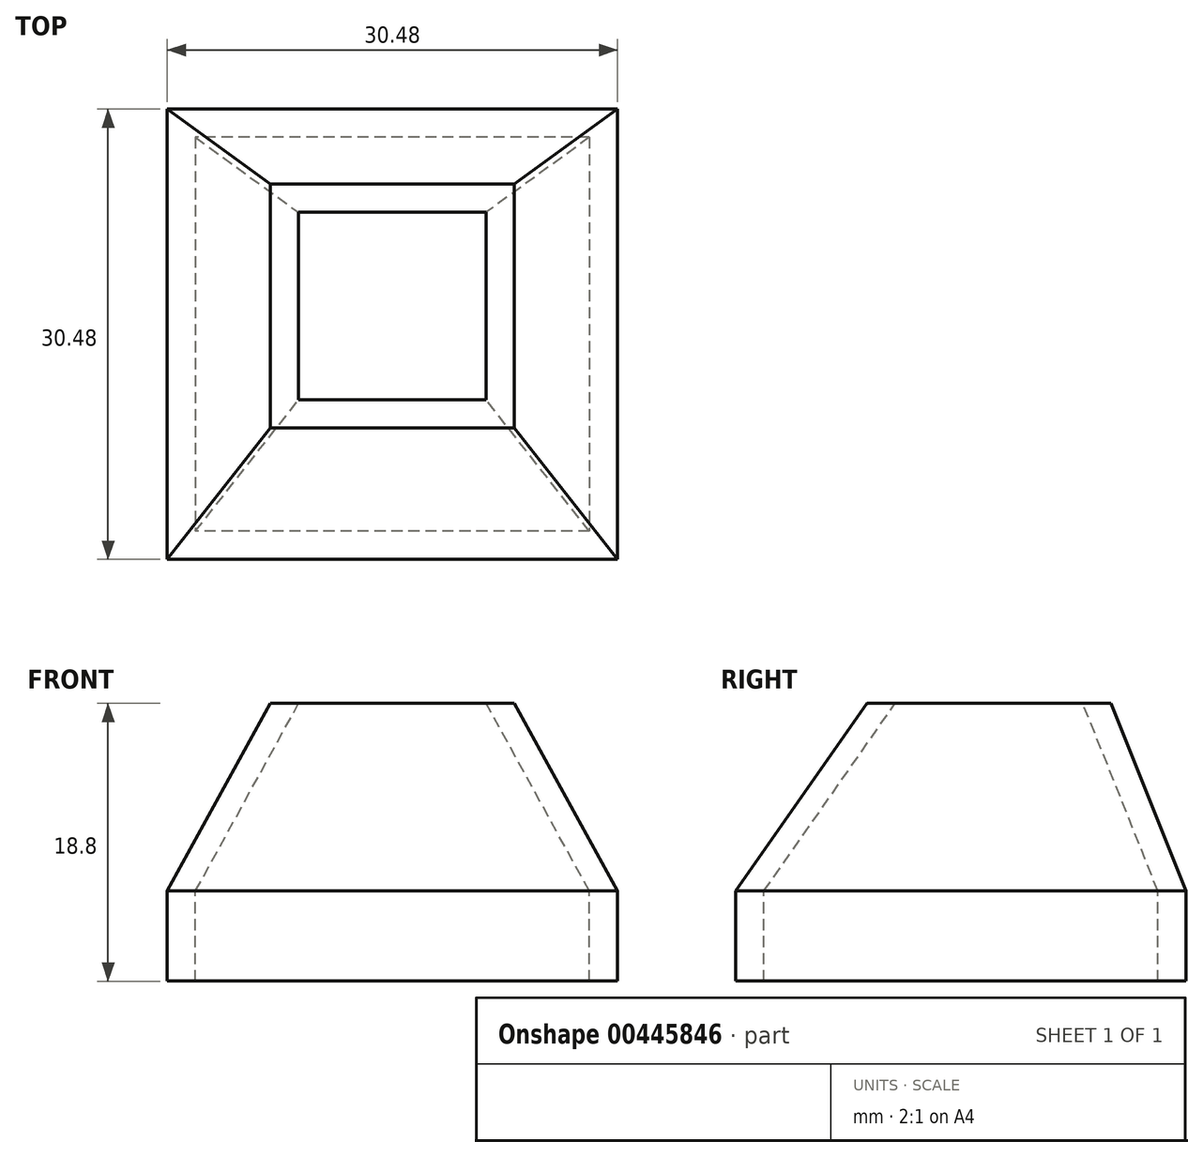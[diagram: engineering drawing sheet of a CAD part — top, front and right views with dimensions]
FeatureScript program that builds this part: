
annotation { "Feature Type Name" : "Feature", "Feature Type Description" : "" }
export const myFeature = defineFeature(function(context is Context, id is Id, definition is map)
    precondition{}
    {
        {
            var Q0;
            Q0=qCreatedBy(makeId("Top.planeOp"),FACE);
            var sketch = newSketch(context, id + "F0", { "sketchPlane" : qUnion([Q0])});
            skLineSegment(sketch, "E0.bottom", {"start": v(13.33, 13.34) * mm, "end": v(-13.34, 13.34) * mm});
            skLineSegment(sketch, "E0.top", {"start": v(13.34, -13.34) * mm, "end": v(-13.33, -13.34) * mm});
            skLineSegment(sketch, "E0.left", {"start": v(13.33, 13.34) * mm, "end": v(13.34, -13.34) * mm});
            skLineSegment(sketch, "E0.right", {"start": v(-13.34, 13.34) * mm, "end": v(-13.33, -13.34) * mm});
            skPoint(sketch, "E0.middle", {"position": v(0, 0) * mm});
            skLineSegment(sketch, "E1.0", {"start": v(15.24, -15.24) * mm, "end": v(-15.24, -15.24) * mm});
            skLineSegment(sketch, "E1.1", {"start": v(15.24, 15.24) * mm, "end": v(15.24, -15.24) * mm});
            skLineSegment(sketch, "E1.2", {"start": v(15.24, 15.24) * mm, "end": v(-15.24, 15.24) * mm});
            skLineSegment(sketch, "E1.3", {"start": v(-15.24, 15.24) * mm, "end": v(-15.24, -15.24) * mm});
            skSolve(sketch);
        }
        {
            var Q0;
            Q0=makeQuery(id+"F0.imprint","IMPRINT",FACE,{"disambiguationData":[TD([[makeQuery(id+"F0.imprint","IMPRINT",EDGE,{"derivedFrom":sQuery(id+"F0.wireOp",EDGE,"E0.bottom")}),-1.0]])]});
            extrude(context, id + "F1", {"entities" : qUnion([Q0]), "oppositeDirection" : true, "depth" : 2.3 * mm});
        }
        {
            var Q0;
            Q0=makeQuery(id+"F0.imprint","IMPRINT",FACE,{"disambiguationData":[TD([[makeQuery(id+"F0.imprint","IMPRINT",EDGE,{"derivedFrom":sQuery(id+"F0.wireOp",EDGE,"E0.bottom")}),-1.0]])]});
            extrude(context, id + "F2", {"entities" : qUnion([Q0]), "operationType" : NewBodyOperationType.ADD, "depth" : 3.8 * mm});
        }
        {
            var Q0;
            Q0=makeQuery(id+"F2.opExtrude","CAP_FACE",FACE,{"disambiguationData":[OSD([sQuery(id+"F0.wireOp",EDGE,"E0.bottom"),sQuery(id+"F0.wireOp",EDGE,"E0.top"),sQuery(id+"F0.wireOp",EDGE,"E0.left"),sQuery(id+"F0.wireOp",EDGE,"E0.right"),sQuery(id+"F0.wireOp",EDGE,"E1.0"),sQuery(id+"F0.wireOp",EDGE,"E1.1"),sQuery(id+"F0.wireOp",EDGE,"E1.2"),sQuery(id+"F0.wireOp",EDGE,"E1.3")])],"isStart":false});
            cPlane(context, id + "F3", {"entities" : qUnion([Q0]), "cplaneType" : CPlaneType.OFFSET, "offset" : 12.7 * mm, "width" : 152.4 * mm, "height" : 152.4 * mm});
        }
        {
            var Q0;
            Q0=qCreatedBy(id+"F3.planeOp",FACE);
            var sketch = newSketch(context, id + "F4", { "sketchPlane" : qUnion([Q0])});
            skLineSegment(sketch, "E2.bottom", {"start": v(6.35, 8.25) * mm, "end": v(-6.35, 8.25) * mm});
            skLineSegment(sketch, "E2.top", {"start": v(6.35, -4.45) * mm, "end": v(-6.35, -4.45) * mm});
            skLineSegment(sketch, "E2.left", {"start": v(6.35, 8.25) * mm, "end": v(6.35, -4.45) * mm});
            skLineSegment(sketch, "E2.right", {"start": v(-6.35, 8.25) * mm, "end": v(-6.35, -4.45) * mm});
            skPoint(sketch, "E2.middle", {"position": v(0, 1.9) * mm});
            skLineSegment(sketch, "E3.0", {"start": v(8.25, -6.35) * mm, "end": v(-8.26, -6.35) * mm});
            skLineSegment(sketch, "E3.1", {"start": v(8.25, 10.16) * mm, "end": v(8.25, -6.35) * mm});
            skLineSegment(sketch, "E3.2", {"start": v(8.25, 10.16) * mm, "end": v(-8.26, 10.16) * mm});
            skLineSegment(sketch, "E3.3", {"start": v(-8.26, 10.16) * mm, "end": v(-8.26, -6.35) * mm});
            skLineSegment(sketch, "E4", {"start": v(-6.35, -4.45) * mm, "end": v(-8.26, -6.35) * mm});
            skLineSegment(sketch, "E5", {"start": v(-6.35, 8.25) * mm, "end": v(-8.26, 10.16) * mm});
            skLineSegment(sketch, "E6", {"start": v(6.35, -4.45) * mm, "end": v(8.25, -6.35) * mm});
            skLineSegment(sketch, "E7", {"start": v(6.35, 8.25) * mm, "end": v(8.25, 10.16) * mm});
            skSolve(sketch);
        }
        {
            var Q0;
            Q0=makeQuery(id+"F2.opExtrude","CAP_FACE",FACE,{"disambiguationData":[OSD([sQuery(id+"F0.wireOp",EDGE,"E0.bottom"),sQuery(id+"F0.wireOp",EDGE,"E0.top"),sQuery(id+"F0.wireOp",EDGE,"E0.left"),sQuery(id+"F0.wireOp",EDGE,"E0.right"),sQuery(id+"F0.wireOp",EDGE,"E1.0"),sQuery(id+"F0.wireOp",EDGE,"E1.1"),sQuery(id+"F0.wireOp",EDGE,"E1.2"),sQuery(id+"F0.wireOp",EDGE,"E1.3")])],"isStart":false});
            var sketch = newSketch(context, id + "F5", { "sketchPlane" : qUnion([Q0])});
            skLineSegment(sketch, "E8.0.0", {"start": v(15.24, 15.24) * mm, "end": v(-15.24, 15.24) * mm});
            skLineSegment(sketch, "E8.0.1", {"start": v(-15.24, 15.24) * mm, "end": v(-15.24, -15.24) * mm});
            skLineSegment(sketch, "E8.0.2", {"start": v(-15.24, -15.24) * mm, "end": v(15.24, -15.24) * mm});
            skLineSegment(sketch, "E8.0.3", {"start": v(15.24, -15.24) * mm, "end": v(15.24, 15.24) * mm});
            skLineSegment(sketch, "E9.0", {"start": v(13.34, -13.34) * mm, "end": v(-13.33, -13.34) * mm});
            skLineSegment(sketch, "E10.0", {"start": v(-13.34, 13.34) * mm, "end": v(-13.33, -13.34) * mm});
            skLineSegment(sketch, "E11.0", {"start": v(13.33, 13.34) * mm, "end": v(13.34, -13.34) * mm});
            skLineSegment(sketch, "E12.0", {"start": v(13.33, 13.34) * mm, "end": v(-13.34, 13.34) * mm});
            skLineSegment(sketch, "E13", {"start": v(-15.24, -15.24) * mm, "end": v(-13.33, -13.34) * mm});
            skLineSegment(sketch, "E14", {"start": v(-15.24, 15.24) * mm, "end": v(-13.34, 13.34) * mm});
            skLineSegment(sketch, "E15", {"start": v(15.24, -15.24) * mm, "end": v(13.34, -13.34) * mm});
            skLineSegment(sketch, "E16", {"start": v(15.24, 15.24) * mm, "end": v(13.33, 13.34) * mm});
            skSolve(sketch);
        }
        {
            var Q1;
            Q1=makeQuery(id+"F5.imprint","IMPRINT",FACE,{"disambiguationData":[TD([[makeQuery(id+"F5.imprint","IMPRINT",EDGE,{"derivedFrom":sQuery(id+"F5.wireOp",EDGE,"E8.0.1")}),1.0]])]});
            var Q2;
            Q2=makeQuery(id+"F4.imprint","IMPRINT",FACE,{"disambiguationData":[TD([[makeQuery(id+"F4.imprint","IMPRINT",EDGE,{"derivedFrom":sQuery(id+"F4.wireOp",EDGE,"E2.right")}),-1.0]])]});
            loft(context, id + "F6", {"operationType" : NewBodyOperationType.ADD, "sheetProfilesArray" : [{ "sheetProfileEntities" : qUnion([Q1]) }, { "sheetProfileEntities" : qUnion([Q2]) }]});
        }
        {
            var Q1;
            Q1=makeQuery(id+"F5.imprint","IMPRINT",FACE,{"disambiguationData":[TD([[makeQuery(id+"F5.imprint","IMPRINT",EDGE,{"derivedFrom":sQuery(id+"F5.wireOp",EDGE,"E8.0.2")}),-1.0]])]});
            var Q2;
            Q2=makeQuery(id+"F4.imprint","IMPRINT",FACE,{"disambiguationData":[TD([[makeQuery(id+"F4.imprint","IMPRINT",EDGE,{"derivedFrom":sQuery(id+"F4.wireOp",EDGE,"E2.top")}),1.0]])]});
            loft(context, id + "F7", {"operationType" : NewBodyOperationType.ADD, "sheetProfilesArray" : [{ "sheetProfileEntities" : qUnion([Q1]) }, { "sheetProfileEntities" : qUnion([Q2]) }]});
        }
        {
            var Q1;
            Q1=makeQuery(id+"F5.imprint","IMPRINT",FACE,{"disambiguationData":[TD([[makeQuery(id+"F5.imprint","IMPRINT",EDGE,{"derivedFrom":sQuery(id+"F5.wireOp",EDGE,"E8.0.3")}),-1.0]])]});
            var Q2;
            Q2=makeQuery(id+"F4.imprint","IMPRINT",FACE,{"disambiguationData":[TD([[makeQuery(id+"F4.imprint","IMPRINT",EDGE,{"derivedFrom":sQuery(id+"F4.wireOp",EDGE,"E2.left")}),1.0]])]});
            loft(context, id + "F8", {"operationType" : NewBodyOperationType.ADD, "sheetProfilesArray" : [{ "sheetProfileEntities" : qUnion([Q1]) }, { "sheetProfileEntities" : qUnion([Q2]) }]});
        }
        {
            var Q1;
            Q1=makeQuery(id+"F5.imprint","IMPRINT",FACE,{"disambiguationData":[TD([[makeQuery(id+"F5.imprint","IMPRINT",EDGE,{"derivedFrom":sQuery(id+"F5.wireOp",EDGE,"E8.0.0")}),1.0]])]});
            var Q2;
            Q2=makeQuery(id+"F4.imprint","IMPRINT",FACE,{"disambiguationData":[TD([[makeQuery(id+"F4.imprint","IMPRINT",EDGE,{"derivedFrom":sQuery(id+"F4.wireOp",EDGE,"E2.bottom")}),-1.0]])]});
            loft(context, id + "F9", {"operationType" : NewBodyOperationType.ADD, "sheetProfilesArray" : [{ "sheetProfileEntities" : qUnion([Q1]) }, { "sheetProfileEntities" : qUnion([Q2]) }]});
        }
    });
